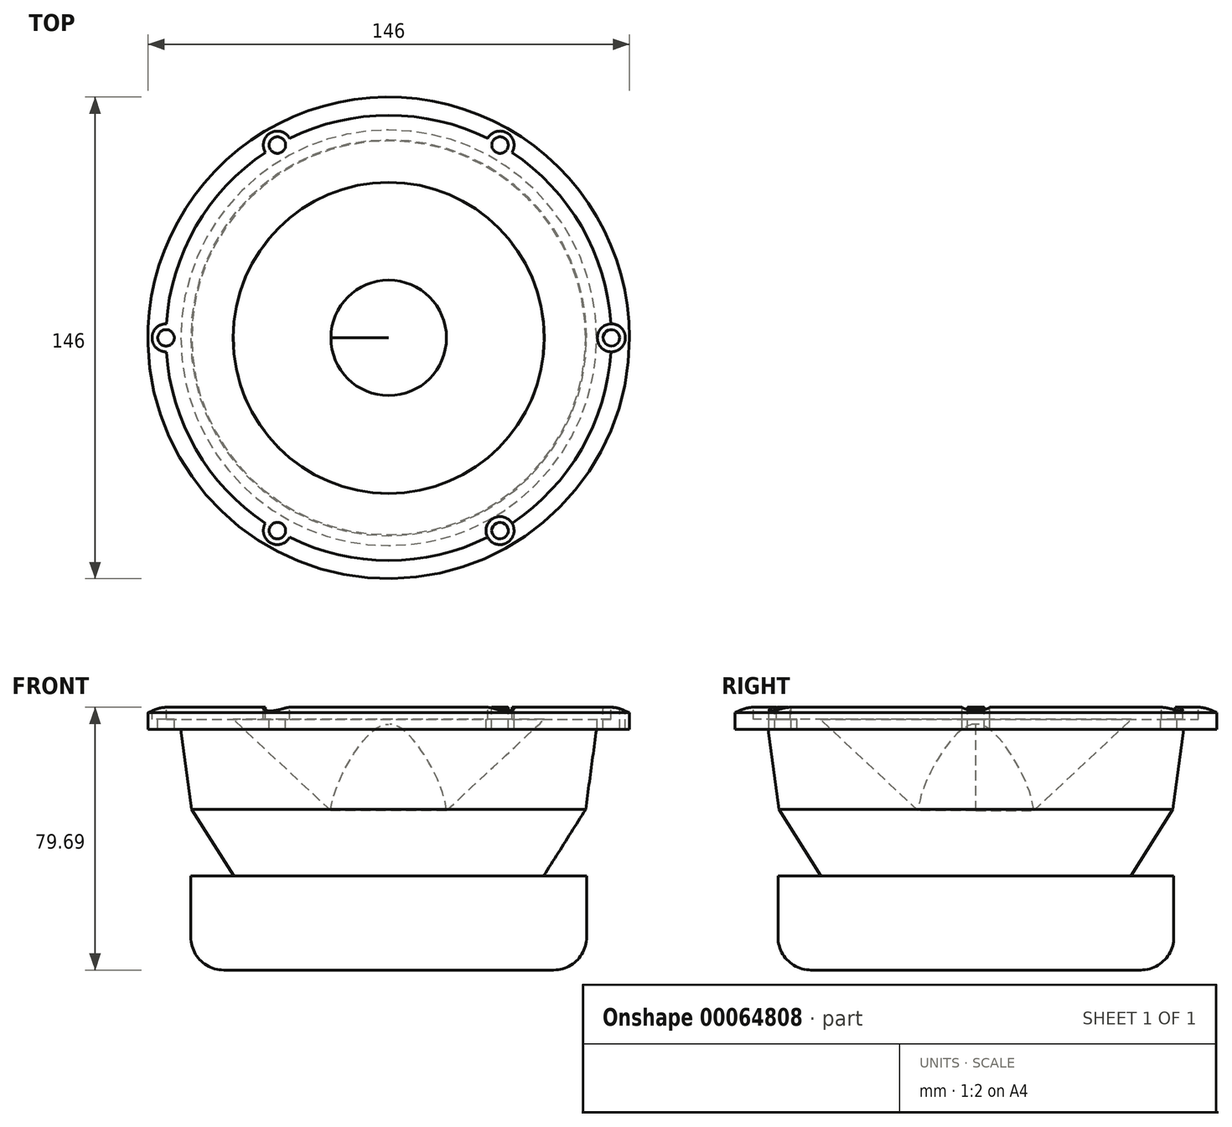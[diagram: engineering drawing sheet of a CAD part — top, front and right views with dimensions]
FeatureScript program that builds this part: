
annotation { "Feature Type Name" : "Feature", "Feature Type Description" : "" }
export const myFeature = defineFeature(function(context is Context, id is Id, definition is map)
    precondition{}
    {
        {
            var Q0;
            Q0=qCreatedBy(makeId("Front.planeOp"),FACE);
            var sketch = newSketch(context, id + "F4", { "sketchPlane" : qUnion([Q0])});
            skLineSegment(sketch, "E0", {"start": v(0, -3.46) * mm, "end": v(0, -78) * mm});
            skArc(sketch, "E1", {"start": v(-49.3, 0) * mm, "mid": v(-55.3, 6) * mm, "end": v(-61.3, 0) * mm});
            skLineSegment(sketch, "E2", {"start": v(-49.3, 0) * mm, "end": v(-17.5, -29.7) * mm});
            skFitSpline(sketch, "E3", {"points": [v(-17.5, -29.7) * mm, v(0, -3.46) * mm, v(13.23, -29.7) * mm], "startDerivative": vector(2.49, 49.73) * mm, "endDerivative": vector(27, -43.23) * mm});
            skLineSegment(sketch, "E4", {"start": v(-73, 0) * mm, "end": v(-73, -5) * mm});
            skLineSegment(sketch, "E5", {"start": v(-73, -5) * mm, "end": v(-63, -5) * mm});
            skLineSegment(sketch, "E6", {"start": v(-63, -5) * mm, "end": v(-59.7, -29.3) * mm});
            skLineSegment(sketch, "E7", {"start": v(-59.7, -29.3) * mm, "end": v(-46.98, -49.43) * mm});
            skLineSegment(sketch, "E8", {"start": v(-46.98, -49.43) * mm, "end": v(-60, -49.43) * mm});
            skLineSegment(sketch, "E9", {"start": v(-60, -49.43) * mm, "end": v(-60, -68) * mm});
            skLineSegment(sketch, "E10", {"start": v(0, -78) * mm, "end": v(-50, -78) * mm});
            skPoint(sketch, "E11.visualSharp", {"position": v(-60, -78) * mm});
            skArc(sketch, "E11.filletArc", {"start": v(-60, -68) * mm, "mid": v(-57.07, -75.07) * mm, "end": v(-50, -78) * mm});
            skLineSegment(sketch, "E12", {"start": v(-73, 0) * mm, "end": v(-71.35, 0.76) * mm});
            skPoint(sketch, "E12.endSnap0", {"position": v(-67.15, 0) * mm});
            skLineSegment(sketch, "E13", {"start": v(-62.94, 0.76) * mm, "end": v(-61.3, 0) * mm});
            skPoint(sketch, "E14.visualSharp", {"position": v(-67.15, 2.71) * mm});
            skArc(sketch, "E14.filletArc", {"start": v(-62.94, 0.76) * mm, "mid": v(-67.15, 1.7) * mm, "end": v(-71.35, 0.76) * mm});
            skSolve(sketch);
        }
        {
            var Q0;
            Q0=makeQuery(id+"F4.imprint","IMPRINT",FACE,{"disambiguationData":[TD([[makeQuery(id+"F4.imprint","IMPRINT",EDGE,{"derivedFrom":sQuery(id+"F4.wireOp",EDGE,"E0")}),-1.0]])]});
            var Q1;
            Q1=sQuery(id+"F4.wireOp",EDGE,"E0");
            revolve(context, id + "F0", {"entities" : qUnion([Q0]), "axis" : qUnion([Q1]), "revolveType" : RevolveType.FULL});
        }
        {
            var Q0;
            Q0=qCreatedBy(makeId("Top.planeOp"),FACE);
            var sketch = newSketch(context, id + "F1", { "sketchPlane" : qUnion([Q0])});
            skCircle(sketch, "E15", {"center": v(0, 0) * mm, "radius": 67.5 * mm});
            skPoint(sketch, "E16", {"position": v(67.5, 0) * mm});
            skPoint(sketch, "E17.1.0", {"position": v(33.75, 58.46) * mm});
            skPoint(sketch, "E17.2.0", {"position": v(-33.75, 58.46) * mm});
            skPoint(sketch, "E18.0.3.0", {"position": v(-67.5, 0) * mm});
            skPoint(sketch, "E18.0.4.0", {"position": v(-33.75, -58.46) * mm});
            skPoint(sketch, "E18.0.5.0", {"position": v(33.75, -58.46) * mm});
            skCircle(sketch, "E19", {"center": v(67.5, 0) * mm, "radius": 4.25 * mm});
            skCircle(sketch, "E20", {"center": v(67.5, 0) * mm, "radius": 2.5 * mm});
            skCircle(sketch, "E21.1.0", {"center": v(33.75, 58.46) * mm, "radius": 2.5 * mm});
            skCircle(sketch, "E21.1.1", {"center": v(33.75, 58.46) * mm, "radius": 4.25 * mm});
            skCircle(sketch, "E21.2.0", {"center": v(-33.75, 58.46) * mm, "radius": 2.5 * mm});
            skCircle(sketch, "E21.2.1", {"center": v(-33.75, 58.46) * mm, "radius": 4.25 * mm});
            skCircle(sketch, "E21.3.0", {"center": v(-67.5, 0) * mm, "radius": 2.5 * mm});
            skCircle(sketch, "E21.3.1", {"center": v(-67.5, 0) * mm, "radius": 4.25 * mm});
            skCircle(sketch, "E21.4.0", {"center": v(-33.75, -58.46) * mm, "radius": 2.5 * mm});
            skCircle(sketch, "E21.4.1", {"center": v(-33.75, -58.46) * mm, "radius": 4.25 * mm});
            skCircle(sketch, "E21.5.0", {"center": v(33.75, -58.46) * mm, "radius": 2.5 * mm});
            skCircle(sketch, "E21.5.1", {"center": v(33.75, -58.46) * mm, "radius": 4.25 * mm});
            skSolve(sketch);
        }
        {
            var Q0;
            {var subQ0=sQuery(id+"F1.wireOp",EDGE,"E21.1.0");var subQ1=sQuery(id+"F1.wireOp",EDGE,"E15");var subQ2=makeQuery(id+"F1.imprint","INTERSECT",VERTEX,{"disambiguationData":[OD(0.0)],"derivedFrom":[subQ1,subQ0]});Q0=makeQuery(id+"F1.imprint","IMPRINT",FACE,{"disambiguationData":[TD([[makeQuery(id+"F1.imprint","IMPRINT",EDGE,{"disambiguationData":[TD([[subQ2,-1.0]])],"derivedFrom":subQ1}),1.0]])]});}
            var Q1;
            {var subQ0=sQuery(id+"F1.wireOp",EDGE,"E21.1.0");var subQ1=sQuery(id+"F1.wireOp",EDGE,"E15");var subQ2=makeQuery(id+"F1.imprint","INTERSECT",VERTEX,{"disambiguationData":[OD(0.0)],"derivedFrom":[subQ1,subQ0]});Q1=makeQuery(id+"F1.imprint","IMPRINT",FACE,{"disambiguationData":[TD([[makeQuery(id+"F1.imprint","IMPRINT",EDGE,{"disambiguationData":[TD([[subQ2,-1.0]])],"derivedFrom":subQ1}),-1.0]])]});}
            var Q2;
            {var subQ0=sQuery(id+"F1.wireOp",EDGE,"E20");var subQ1=sQuery(id+"F1.wireOp",EDGE,"E15");var subQ2=makeQuery(id+"F1.imprint","INTERSECT",VERTEX,{"disambiguationData":[OD(0.0)],"derivedFrom":[subQ1,subQ0]});Q2=makeQuery(id+"F1.imprint","IMPRINT",FACE,{"disambiguationData":[TD([[makeQuery(id+"F1.imprint","IMPRINT",EDGE,{"disambiguationData":[TD([[subQ2,-1.0]])],"derivedFrom":subQ1}),1.0]])]});}
            var Q3;
            {var subQ0=sQuery(id+"F1.wireOp",EDGE,"E20");var subQ1=sQuery(id+"F1.wireOp",EDGE,"E15");var subQ2=makeQuery(id+"F1.imprint","INTERSECT",VERTEX,{"disambiguationData":[OD(0.0)],"derivedFrom":[subQ1,subQ0]});Q3=makeQuery(id+"F1.imprint","IMPRINT",FACE,{"disambiguationData":[TD([[makeQuery(id+"F1.imprint","IMPRINT",EDGE,{"disambiguationData":[TD([[subQ2,-1.0]])],"derivedFrom":subQ1}),-1.0]])]});}
            var Q4;
            {var subQ0=sQuery(id+"F1.wireOp",EDGE,"E21.5.0");var subQ1=sQuery(id+"F1.wireOp",EDGE,"E15");var subQ2=makeQuery(id+"F1.imprint","INTERSECT",VERTEX,{"disambiguationData":[OD(0.0)],"derivedFrom":[subQ1,subQ0]});Q4=makeQuery(id+"F1.imprint","IMPRINT",FACE,{"disambiguationData":[TD([[makeQuery(id+"F1.imprint","IMPRINT",EDGE,{"disambiguationData":[TD([[subQ2,1.0]])],"derivedFrom":subQ1}),1.0]])]});}
            var Q5;
            {var subQ0=sQuery(id+"F1.wireOp",EDGE,"E21.5.0");var subQ1=sQuery(id+"F1.wireOp",EDGE,"E15");var subQ2=makeQuery(id+"F1.imprint","INTERSECT",VERTEX,{"disambiguationData":[OD(0.0)],"derivedFrom":[subQ1,subQ0]});Q5=makeQuery(id+"F1.imprint","IMPRINT",FACE,{"disambiguationData":[TD([[makeQuery(id+"F1.imprint","IMPRINT",EDGE,{"disambiguationData":[TD([[subQ2,1.0]])],"derivedFrom":subQ1}),-1.0]])]});}
            var Q6;
            {var subQ0=sQuery(id+"F1.wireOp",EDGE,"E21.4.0");var subQ1=sQuery(id+"F1.wireOp",EDGE,"E15");var subQ2=makeQuery(id+"F1.imprint","INTERSECT",VERTEX,{"disambiguationData":[OD(0.0)],"derivedFrom":[subQ1,subQ0]});Q6=makeQuery(id+"F1.imprint","IMPRINT",FACE,{"disambiguationData":[TD([[makeQuery(id+"F1.imprint","IMPRINT",EDGE,{"disambiguationData":[TD([[subQ2,-1.0]])],"derivedFrom":subQ1}),-1.0]])]});}
            var Q7;
            {var subQ0=sQuery(id+"F1.wireOp",EDGE,"E21.4.0");var subQ1=sQuery(id+"F1.wireOp",EDGE,"E15");var subQ2=makeQuery(id+"F1.imprint","INTERSECT",VERTEX,{"disambiguationData":[OD(0.0)],"derivedFrom":[subQ1,subQ0]});Q7=makeQuery(id+"F1.imprint","IMPRINT",FACE,{"disambiguationData":[TD([[makeQuery(id+"F1.imprint","IMPRINT",EDGE,{"disambiguationData":[TD([[subQ2,-1.0]])],"derivedFrom":subQ1}),1.0]])]});}
            var Q8;
            {var subQ0=sQuery(id+"F1.wireOp",EDGE,"E21.3.0");var subQ1=sQuery(id+"F1.wireOp",EDGE,"E15");var subQ2=makeQuery(id+"F1.imprint","INTERSECT",VERTEX,{"disambiguationData":[OD(0.0)],"derivedFrom":[subQ1,subQ0]});Q8=makeQuery(id+"F1.imprint","IMPRINT",FACE,{"disambiguationData":[TD([[makeQuery(id+"F1.imprint","IMPRINT",EDGE,{"disambiguationData":[TD([[subQ2,-1.0]])],"derivedFrom":subQ1}),-1.0]])]});}
            var Q9;
            {var subQ0=sQuery(id+"F1.wireOp",EDGE,"E21.3.0");var subQ1=sQuery(id+"F1.wireOp",EDGE,"E15");var subQ2=makeQuery(id+"F1.imprint","INTERSECT",VERTEX,{"disambiguationData":[OD(0.0)],"derivedFrom":[subQ1,subQ0]});Q9=makeQuery(id+"F1.imprint","IMPRINT",FACE,{"disambiguationData":[TD([[makeQuery(id+"F1.imprint","IMPRINT",EDGE,{"disambiguationData":[TD([[subQ2,-1.0]])],"derivedFrom":subQ1}),1.0]])]});}
            var Q10;
            {var subQ0=sQuery(id+"F1.wireOp",EDGE,"E21.2.0");var subQ1=sQuery(id+"F1.wireOp",EDGE,"E15");var subQ2=makeQuery(id+"F1.imprint","INTERSECT",VERTEX,{"disambiguationData":[OD(0.0)],"derivedFrom":[subQ1,subQ0]});Q10=makeQuery(id+"F1.imprint","IMPRINT",FACE,{"disambiguationData":[TD([[makeQuery(id+"F1.imprint","IMPRINT",EDGE,{"disambiguationData":[TD([[subQ2,-1.0]])],"derivedFrom":subQ1}),-1.0]])]});}
            var Q11;
            {var subQ0=sQuery(id+"F1.wireOp",EDGE,"E21.2.0");var subQ1=sQuery(id+"F1.wireOp",EDGE,"E15");var subQ2=makeQuery(id+"F1.imprint","INTERSECT",VERTEX,{"disambiguationData":[OD(0.0)],"derivedFrom":[subQ1,subQ0]});Q11=makeQuery(id+"F1.imprint","IMPRINT",FACE,{"disambiguationData":[TD([[makeQuery(id+"F1.imprint","IMPRINT",EDGE,{"disambiguationData":[TD([[subQ2,-1.0]])],"derivedFrom":subQ1}),1.0]])]});}
            extrude(context, id + "F2", {"entities" : qUnion([Q0, Q1, Q2, Q3, Q4, Q5, Q6, Q7, Q8, Q9, Q10, Q11]), "operationType" : NewBodyOperationType.REMOVE, "endBound" : BoundingType.THROUGH_ALL, "oppositeDirection" : true, "depth" : 25 * mm, "hasSecondDirection" : true, "secondDirectionBound" : BoundingType.THROUGH_ALL, "secondDirectionOppositeDirection" : false, "secondDirectionDepth" : 25 * mm});
        }
        {
            var Q0;
            {var subQ0=sQuery(id+"F1.wireOp",EDGE,"E21.3.1");var subQ1=sQuery(id+"F1.wireOp",EDGE,"E15");var subQ2=makeQuery(id+"F1.imprint","INTERSECT",VERTEX,{"disambiguationData":[OD(0.0)],"derivedFrom":[subQ1,subQ0]});Q0=makeQuery(id+"F1.imprint","IMPRINT",FACE,{"disambiguationData":[TD([[makeQuery(id+"F1.imprint","IMPRINT",EDGE,{"disambiguationData":[TD([[subQ2,-1.0]])],"derivedFrom":subQ1}),1.0]])]});}
            var Q1;
            {var subQ0=sQuery(id+"F1.wireOp",EDGE,"E21.3.1");var subQ1=sQuery(id+"F1.wireOp",EDGE,"E15");var subQ2=makeQuery(id+"F1.imprint","INTERSECT",VERTEX,{"disambiguationData":[OD(0.0)],"derivedFrom":[subQ1,subQ0]});Q1=makeQuery(id+"F1.imprint","IMPRINT",FACE,{"disambiguationData":[TD([[makeQuery(id+"F1.imprint","IMPRINT",EDGE,{"disambiguationData":[TD([[subQ2,-1.0]])],"derivedFrom":subQ1}),-1.0]])]});}
            var Q2;
            {var subQ0=sQuery(id+"F1.wireOp",EDGE,"E21.2.1");var subQ1=sQuery(id+"F1.wireOp",EDGE,"E15");var subQ2=makeQuery(id+"F1.imprint","INTERSECT",VERTEX,{"disambiguationData":[OD(0.0)],"derivedFrom":[subQ1,subQ0]});Q2=makeQuery(id+"F1.imprint","IMPRINT",FACE,{"disambiguationData":[TD([[makeQuery(id+"F1.imprint","IMPRINT",EDGE,{"disambiguationData":[TD([[subQ2,-1.0]])],"derivedFrom":subQ1}),1.0]])]});}
            var Q3;
            {var subQ0=sQuery(id+"F1.wireOp",EDGE,"E21.2.1");var subQ1=sQuery(id+"F1.wireOp",EDGE,"E15");var subQ2=makeQuery(id+"F1.imprint","INTERSECT",VERTEX,{"disambiguationData":[OD(0.0)],"derivedFrom":[subQ1,subQ0]});Q3=makeQuery(id+"F1.imprint","IMPRINT",FACE,{"disambiguationData":[TD([[makeQuery(id+"F1.imprint","IMPRINT",EDGE,{"disambiguationData":[TD([[subQ2,-1.0]])],"derivedFrom":subQ1}),-1.0]])]});}
            var Q4;
            {var subQ0=sQuery(id+"F1.wireOp",EDGE,"E21.1.1");var subQ1=sQuery(id+"F1.wireOp",EDGE,"E15");var subQ2=makeQuery(id+"F1.imprint","INTERSECT",VERTEX,{"disambiguationData":[OD(0.0)],"derivedFrom":[subQ1,subQ0]});Q4=makeQuery(id+"F1.imprint","IMPRINT",FACE,{"disambiguationData":[TD([[makeQuery(id+"F1.imprint","IMPRINT",EDGE,{"disambiguationData":[TD([[subQ2,-1.0]])],"derivedFrom":subQ1}),-1.0]])]});}
            var Q5;
            {var subQ0=sQuery(id+"F1.wireOp",EDGE,"E21.1.1");var subQ1=sQuery(id+"F1.wireOp",EDGE,"E15");var subQ2=makeQuery(id+"F1.imprint","INTERSECT",VERTEX,{"disambiguationData":[OD(0.0)],"derivedFrom":[subQ1,subQ0]});Q5=makeQuery(id+"F1.imprint","IMPRINT",FACE,{"disambiguationData":[TD([[makeQuery(id+"F1.imprint","IMPRINT",EDGE,{"disambiguationData":[TD([[subQ2,-1.0]])],"derivedFrom":subQ1}),1.0]])]});}
            var Q6;
            {var subQ0=sQuery(id+"F1.wireOp",EDGE,"E19");var subQ1=sQuery(id+"F1.wireOp",EDGE,"E15");var subQ2=makeQuery(id+"F1.imprint","INTERSECT",VERTEX,{"disambiguationData":[OD(0.0)],"derivedFrom":[subQ1,subQ0]});Q6=makeQuery(id+"F1.imprint","IMPRINT",FACE,{"disambiguationData":[TD([[makeQuery(id+"F1.imprint","IMPRINT",EDGE,{"disambiguationData":[TD([[subQ2,-1.0]])],"derivedFrom":subQ1}),-1.0]])]});}
            var Q7;
            {var subQ0=sQuery(id+"F1.wireOp",EDGE,"E19");var subQ1=sQuery(id+"F1.wireOp",EDGE,"E15");var subQ2=makeQuery(id+"F1.imprint","INTERSECT",VERTEX,{"disambiguationData":[OD(0.0)],"derivedFrom":[subQ1,subQ0]});Q7=makeQuery(id+"F1.imprint","IMPRINT",FACE,{"disambiguationData":[TD([[makeQuery(id+"F1.imprint","IMPRINT",EDGE,{"disambiguationData":[TD([[subQ2,-1.0]])],"derivedFrom":subQ1}),1.0]])]});}
            var Q8;
            {var subQ0=sQuery(id+"F1.wireOp",EDGE,"E21.5.1");var subQ1=sQuery(id+"F1.wireOp",EDGE,"E15");var subQ2=makeQuery(id+"F1.imprint","INTERSECT",VERTEX,{"disambiguationData":[OD(0.0)],"derivedFrom":[subQ1,subQ0]});Q8=makeQuery(id+"F1.imprint","IMPRINT",FACE,{"disambiguationData":[TD([[makeQuery(id+"F1.imprint","IMPRINT",EDGE,{"disambiguationData":[TD([[subQ2,1.0]])],"derivedFrom":subQ1}),-1.0]])]});}
            var Q9;
            {var subQ0=sQuery(id+"F1.wireOp",EDGE,"E21.5.1");var subQ1=sQuery(id+"F1.wireOp",EDGE,"E15");var subQ2=makeQuery(id+"F1.imprint","INTERSECT",VERTEX,{"disambiguationData":[OD(0.0)],"derivedFrom":[subQ1,subQ0]});Q9=makeQuery(id+"F1.imprint","IMPRINT",FACE,{"disambiguationData":[TD([[makeQuery(id+"F1.imprint","IMPRINT",EDGE,{"disambiguationData":[TD([[subQ2,1.0]])],"derivedFrom":subQ1}),1.0]])]});}
            var Q10;
            {var subQ0=sQuery(id+"F1.wireOp",EDGE,"E21.4.1");var subQ1=sQuery(id+"F1.wireOp",EDGE,"E15");var subQ2=makeQuery(id+"F1.imprint","INTERSECT",VERTEX,{"disambiguationData":[OD(0.0)],"derivedFrom":[subQ1,subQ0]});Q10=makeQuery(id+"F1.imprint","IMPRINT",FACE,{"disambiguationData":[TD([[makeQuery(id+"F1.imprint","IMPRINT",EDGE,{"disambiguationData":[TD([[subQ2,-1.0]])],"derivedFrom":subQ1}),-1.0]])]});}
            var Q11;
            {var subQ0=sQuery(id+"F1.wireOp",EDGE,"E21.4.1");var subQ1=sQuery(id+"F1.wireOp",EDGE,"E15");var subQ2=makeQuery(id+"F1.imprint","INTERSECT",VERTEX,{"disambiguationData":[OD(0.0)],"derivedFrom":[subQ1,subQ0]});Q11=makeQuery(id+"F1.imprint","IMPRINT",FACE,{"disambiguationData":[TD([[makeQuery(id+"F1.imprint","IMPRINT",EDGE,{"disambiguationData":[TD([[subQ2,-1.0]])],"derivedFrom":subQ1}),1.0]])]});}
            extrude(context, id + "F3", {"entities" : qUnion([Q0, Q1, Q2, Q3, Q4, Q5, Q6, Q7, Q8, Q9, Q10, Q11]), "operationType" : NewBodyOperationType.REMOVE, "oppositeDirection" : true, "depth" : 2 * mm, "hasSecondDirection" : true, "secondDirectionBound" : BoundingType.THROUGH_ALL, "secondDirectionOppositeDirection" : false, "secondDirectionDepth" : 25 * mm});
        }
    });
